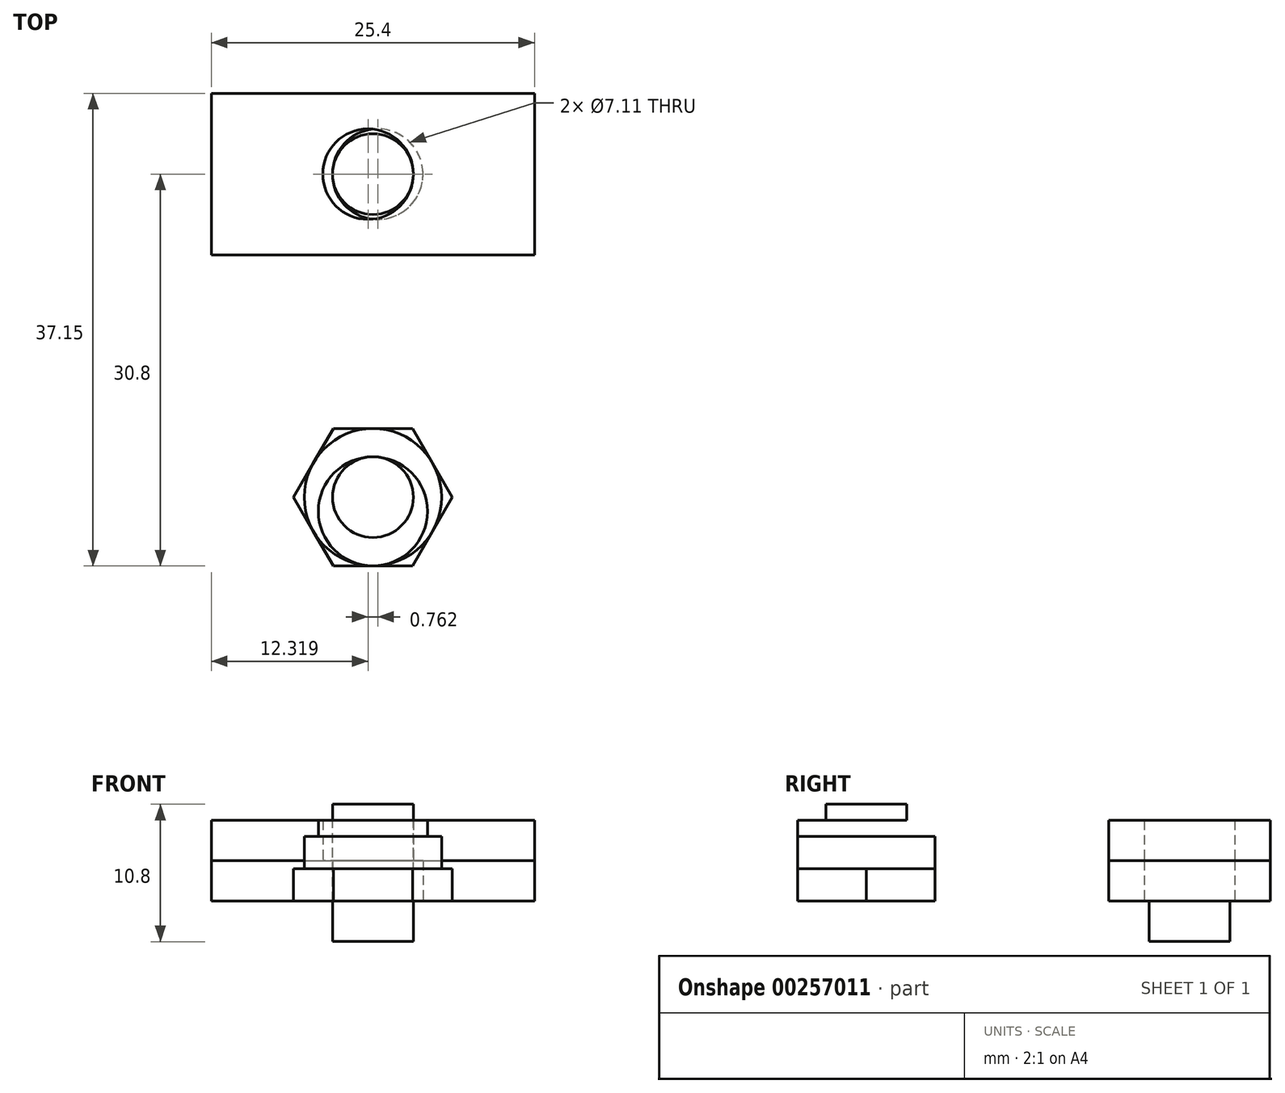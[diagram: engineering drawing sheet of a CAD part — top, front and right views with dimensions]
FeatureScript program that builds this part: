
annotation { "Feature Type Name" : "Feature", "Feature Type Description" : "" }
export const myFeature = defineFeature(function(context is Context, id is Id, definition is map)
    precondition{}
    {
        {
            var Q0;
            Q0=qCreatedBy(makeId("Top.planeOp"),FACE);
            var sketch = newSketch(context, id + "F0", { "sketchPlane" : qUnion([Q0])});
            skLineSegment(sketch, "E0.bottom", {"start": v(-12.7, 6.35) * mm, "end": v(12.7, 6.35) * mm});
            skLineSegment(sketch, "E0.top", {"start": v(-12.7, -6.35) * mm, "end": v(12.7, -6.35) * mm});
            skLineSegment(sketch, "E0.left", {"start": v(-12.7, 6.35) * mm, "end": v(-12.7, -6.35) * mm});
            skLineSegment(sketch, "E0.right", {"start": v(12.7, 6.35) * mm, "end": v(12.7, -6.35) * mm});
            skLineSegment(sketch, "E1", {"start": v(0, 6.35) * mm, "end": v(0, -6.35) * mm});
            skLineSegment(sketch, "E2", {"start": v(12.7, 0) * mm, "end": v(-12.7, 0) * mm});
            skPoint(sketch, "E3", {"position": v(0, 0) * mm});
            skCircle(sketch, "E4", {"center": v(0.38, 0) * mm, "radius": 3.56 * mm});
            skSolve(sketch);
        }
        {
            var Q0;
            Q0 = qSketchRegion(id + "F0", true);
            extrude(context, id + "F1", {"entities" : qUnion([Q0]), "depth" : 3.17 * mm});
        }
        {
            var Q0;
            Q0=makeQuery(id+"F1.opExtrude","CAP_FACE",FACE,{"disambiguationData":[OSD([sQuery(id+"F0.wireOp",EDGE,"E0.bottom"),sQuery(id+"F0.wireOp",EDGE,"E0.top"),sQuery(id+"F0.wireOp",EDGE,"E0.left"),sQuery(id+"F0.wireOp",EDGE,"E0.right"),sQuery(id+"F0.wireOp",EDGE,"E4")])],"isStart":false});
            var sketch = newSketch(context, id + "F2", { "sketchPlane" : qUnion([Q0])});
            skLineSegment(sketch, "E5.bottom", {"start": v(-12.7, 6.35) * mm, "end": v(12.7, 6.35) * mm});
            skLineSegment(sketch, "E5.top", {"start": v(-12.7, -6.35) * mm, "end": v(12.7, -6.35) * mm});
            skLineSegment(sketch, "E5.left", {"start": v(-12.7, 6.35) * mm, "end": v(-12.7, -6.35) * mm});
            skLineSegment(sketch, "E5.right", {"start": v(12.7, 6.35) * mm, "end": v(12.7, -6.35) * mm});
            skCircle(sketch, "E6", {"center": v(-0.38, 0) * mm, "radius": 3.56 * mm});
            skSolve(sketch);
        }
        {
            var Q0;
            Q0 = qSketchRegion(id + "F2", true);
            extrude(context, id + "F3", {"entities" : qUnion([Q0]), "depth" : 3.17 * mm});
        }
        {
            var Q0;
            Q0=makeQuery(id+"F3.opExtrude","CAP_FACE",FACE,{"disambiguationData":[OSD([sQuery(id+"F2.wireOp",EDGE,"E5.bottom"),sQuery(id+"F2.wireOp",EDGE,"E5.top"),sQuery(id+"F2.wireOp",EDGE,"E5.left"),sQuery(id+"F2.wireOp",EDGE,"E5.right"),sQuery(id+"F2.wireOp",EDGE,"E6")])],"isStart":false});
            var sketch = newSketch(context, id + "F4", { "sketchPlane" : qUnion([Q0])});
            skCircle(sketch, "E7", {"center": v(0, 0) * mm, "radius": 3.17 * mm});
            skSolve(sketch);
        }
        {
            var Q0;
            Q0 = qSketchRegion(id + "F4", true);
            extrude(context, id + "F5", {"entities" : qUnion([Q0]), "oppositeDirection" : true, "depth" : 9.52 * mm});
        }
        {
            var Q0;
            Q0=qCreatedBy(makeId("Top.planeOp"),FACE);
            var sketch = newSketch(context, id + "F6", { "sketchPlane" : qUnion([Q0])});
            skCircle(sketch, "E8.cCircle", {"center": v(0, -25.4) * mm, "radius": 5.4 * mm, "construction": true});
            skLineSegment(sketch, "E8.0", {"start": v(6.23, -25.4) * mm, "end": v(3.12, -30.8) * mm});
            skLineSegment(sketch, "E8.1", {"start": v(3.12, -30.8) * mm, "end": v(-3.12, -30.8) * mm});
            skLineSegment(sketch, "E8.2", {"start": v(-3.12, -30.8) * mm, "end": v(-6.23, -25.4) * mm});
            skLineSegment(sketch, "E8.3", {"start": v(-6.23, -25.4) * mm, "end": v(-3.12, -20) * mm});
            skLineSegment(sketch, "E8.4", {"start": v(-3.12, -20) * mm, "end": v(3.12, -20) * mm});
            skLineSegment(sketch, "E8.5", {"start": v(3.12, -20) * mm, "end": v(6.23, -25.4) * mm});
            skPoint(sketch, "E8.0.midPoint", {"position": v(4.67, -28.1) * mm});
            skSolve(sketch);
        }
        {
            var Q0;
            Q0=makeQuery(id+"F6.imprint","IMPRINT",FACE,{"disambiguationData":[TD([[makeQuery(id+"F6.imprint","IMPRINT",EDGE,{"derivedFrom":sQuery(id+"F6.wireOp",EDGE,"E8.0")}),-1.0]])]});
            extrude(context, id + "F7", {"entities" : qUnion([Q0]), "depth" : 2.54 * mm});
        }
        {
            var Q0;
            Q0=makeQuery(id+"F7.opExtrude","CAP_FACE",FACE,{"disambiguationData":[OSD([sQuery(id+"F6.wireOp",EDGE,"E8.0"),sQuery(id+"F6.wireOp",EDGE,"E8.1"),sQuery(id+"F6.wireOp",EDGE,"E8.2"),sQuery(id+"F6.wireOp",EDGE,"E8.3"),sQuery(id+"F6.wireOp",EDGE,"E8.4"),sQuery(id+"F6.wireOp",EDGE,"E8.5")])],"isStart":false});
            var sketch = newSketch(context, id + "F8", { "sketchPlane" : qUnion([Q0])});
            skCircle(sketch, "E9", {"center": v(0, -25.4) * mm, "radius": 5.4 * mm});
            skSolve(sketch);
        }
        {
            var Q0;
            Q0 = qSketchRegion(id + "F8", true);
            extrude(context, id + "F9", {"entities" : qUnion([Q0]), "operationType" : NewBodyOperationType.ADD, "depth" : 2.54 * mm});
        }
        {
            var Q0;
            Q0=makeQuery(id+"F9.opExtrude","CAP_FACE",FACE,{"disambiguationData":[OSD([sQuery(id+"F8.wireOp",EDGE,"E9")])],"isStart":false});
            var sketch = newSketch(context, id + "F10", { "sketchPlane" : qUnion([Q0])});
            skCircle(sketch, "E10", {"center": v(0, -25.4) * mm, "radius": 3.18 * mm});
            skSolve(sketch);
        }
        {
            var Q0;
            Q0=makeQuery(id+"F10.imprint","IMPRINT",FACE,{"disambiguationData":[TD([[makeQuery(id+"F10.imprint","IMPRINT",EDGE,{"derivedFrom":sQuery(id+"F10.wireOp",EDGE,"E10")}),1.0]])]});
            extrude(context, id + "F11", {"entities" : qUnion([Q0]), "operationType" : NewBodyOperationType.ADD, "depth" : 2.54 * mm});
        }
        {
            var Q0;
            Q0=makeQuery(id+"F9.opExtrude","CAP_FACE",FACE,{"disambiguationData":[OSD([sQuery(id+"F8.wireOp",EDGE,"E9")])],"isStart":false});
            var sketch = newSketch(context, id + "F12", { "sketchPlane" : qUnion([Q0])});
            skCircle(sketch, "E11", {"center": v(0, -26.51) * mm, "radius": 4.29 * mm});
            skSolve(sketch);
        }
        {
            var Q0;
            Q0 = qSketchRegion(id + "F12", true);
            extrude(context, id + "F13", {"entities" : qUnion([Q0]), "operationType" : NewBodyOperationType.ADD, "depth" : 1.27 * mm});
        }
    });
